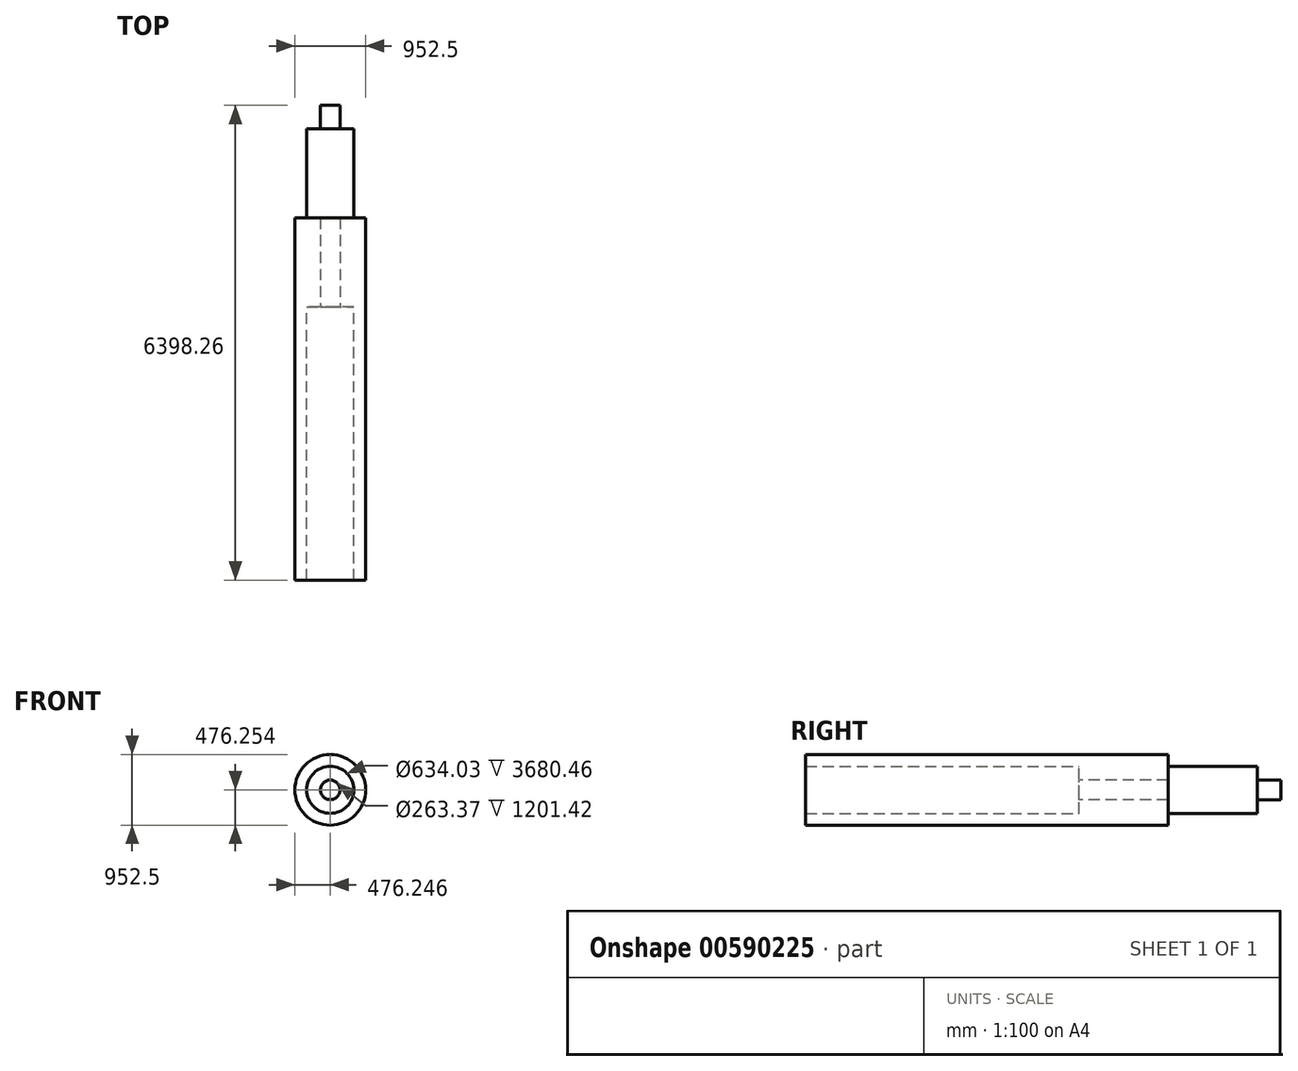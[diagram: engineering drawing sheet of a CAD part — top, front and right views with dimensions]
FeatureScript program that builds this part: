
annotation { "Feature Type Name" : "Feature", "Feature Type Description" : "" }
export const myFeature = defineFeature(function(context is Context, id is Id, definition is map)
    precondition{}
    {
        {
            var Q0;
            Q0=qCreatedBy(makeId("Front.planeOp"),FACE);
            var sketch = newSketch(context, id + "F0", { "sketchPlane" : qUnion([Q0])});
            skCircle(sketch, "E0", {"center": v(-463.18, 650.68) * mm, "radius": 476.25 * mm});
            skCircle(sketch, "E1", {"center": v(-463.18, 650.68) * mm, "radius": 317.01 * mm});
            skCircle(sketch, "E2", {"center": v(-463.18, 650.68) * mm, "radius": 131.68 * mm});
            skSolve(sketch);
        }
        {
            var Q0;
            Q0 = qSketchRegion(id + "F0", true);
            extrude(context, id + "F1", {"entities" : qUnion([Q0]), "depth" : 4881.88 * mm, "offsetDistance" : 25.4 * mm});
        }
        {
            var Q0;
            Q0=makeQuery(id+"F0.imprint","IMPRINT",FACE,{"disambiguationData":[TD([[makeQuery(id+"F0.imprint","IMPRINT",EDGE,{"derivedFrom":sQuery(id+"F0.wireOp",EDGE,"E1")}),1.0]])]});
            extrude(context, id + "F2", {"entities" : qUnion([Q0]), "operationType" : NewBodyOperationType.ADD, "endBound" : BoundingType.SYMMETRIC, "oppositeDirection" : true, "depth" : 2402.84 * mm, "offsetDistance" : 25.4 * mm});
        }
        {
            var Q0;
            Q0=makeQuery(id+"F0.imprint","IMPRINT",FACE,{"disambiguationData":[TD([[makeQuery(id+"F0.imprint","IMPRINT",EDGE,{"derivedFrom":sQuery(id+"F0.wireOp",EDGE,"E2")}),1.0]])]});
            extrude(context, id + "F3", {"entities" : qUnion([Q0]), "operationType" : NewBodyOperationType.ADD, "oppositeDirection" : true, "depth" : 1516.38 * mm, "offsetDistance" : 25.4 * mm});
        }
    });
